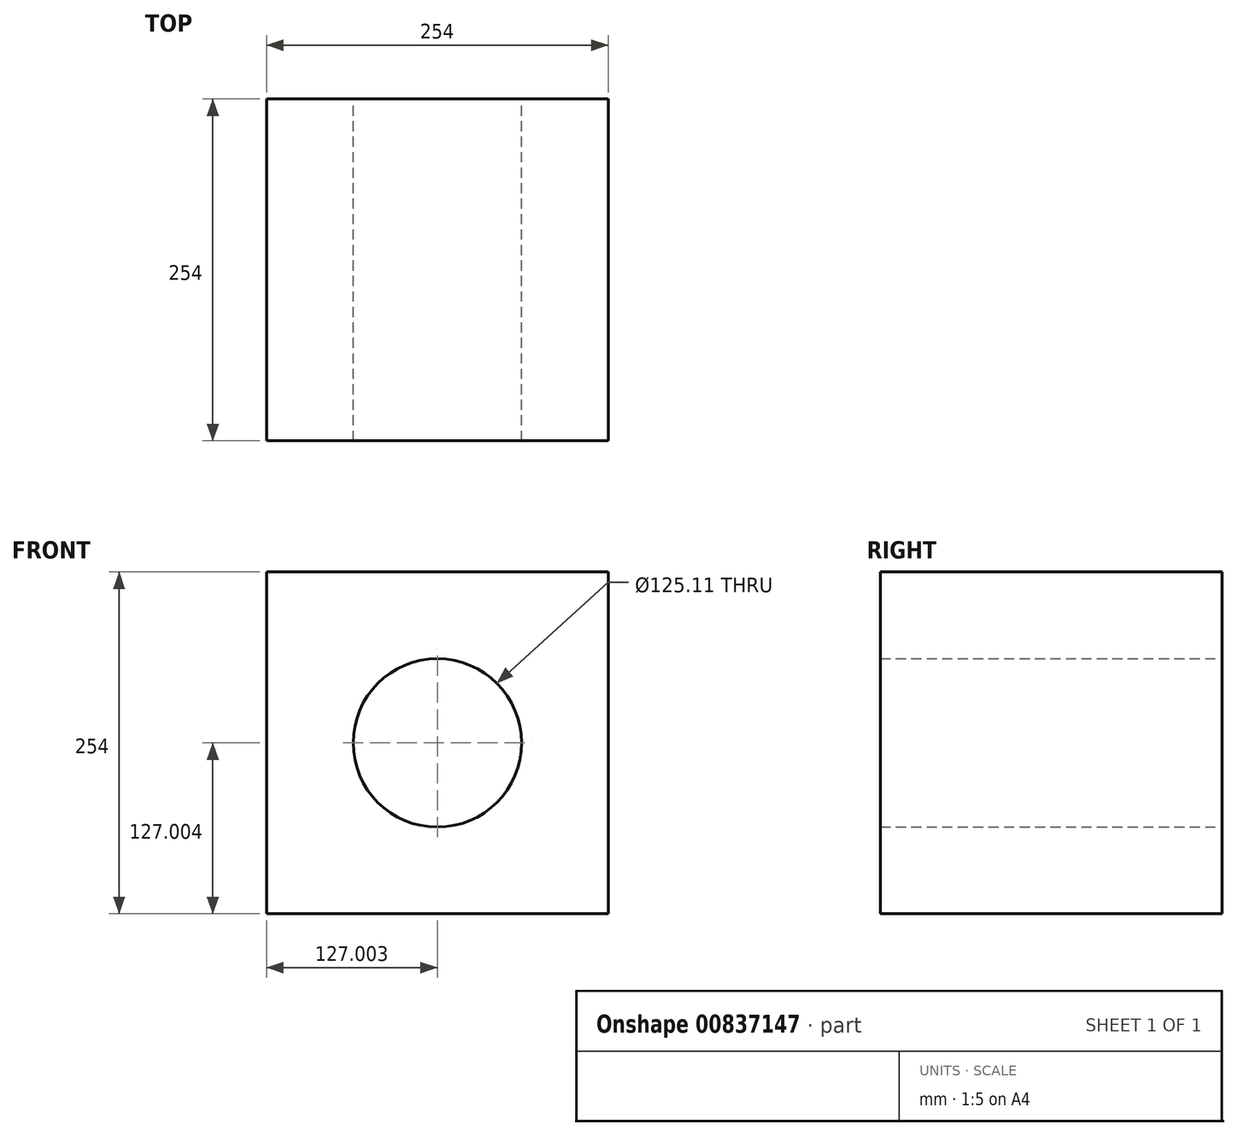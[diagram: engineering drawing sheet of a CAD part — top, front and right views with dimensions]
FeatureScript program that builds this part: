
annotation { "Feature Type Name" : "Feature", "Feature Type Description" : "" }
export const myFeature = defineFeature(function(context is Context, id is Id, definition is map)
    precondition{}
    {
        {
            var Q0;
            Q0=qCreatedBy(makeId("Front.planeOp"),FACE);
            var sketch = newSketch(context, id + "F0", { "sketchPlane" : qUnion([Q0])});
            skLineSegment(sketch, "E0.bottom", {"start": v(71.95, 242.68) * mm, "end": v(-182.05, 242.68) * mm});
            skLineSegment(sketch, "E0.top", {"start": v(71.95, -11.32) * mm, "end": v(-182.05, -11.32) * mm});
            skLineSegment(sketch, "E0.left", {"start": v(71.95, 242.68) * mm, "end": v(71.95, -11.32) * mm});
            skLineSegment(sketch, "E0.right", {"start": v(-182.05, 242.68) * mm, "end": v(-182.05, -11.32) * mm});
            skPoint(sketch, "E0.middle", {"position": v(-55.05, 115.68) * mm});
            skCircle(sketch, "E1", {"center": v(-55.05, 115.68) * mm, "radius": 62.56 * mm});
            skSolve(sketch);
        }
        {
            var Q0;
            Q0=makeQuery(id+"F0.imprint","IMPRINT",FACE,{"disambiguationData":[TD([[makeQuery(id+"F0.imprint","IMPRINT",EDGE,{"derivedFrom":sQuery(id+"F0.wireOp",EDGE,"E0.bottom")}),1.0]])]});
            extrude(context, id + "F1", {"entities" : qUnion([Q0]), "depth" : 254 * mm, "offsetDistance" : 25.4 * mm});
        }
    });
